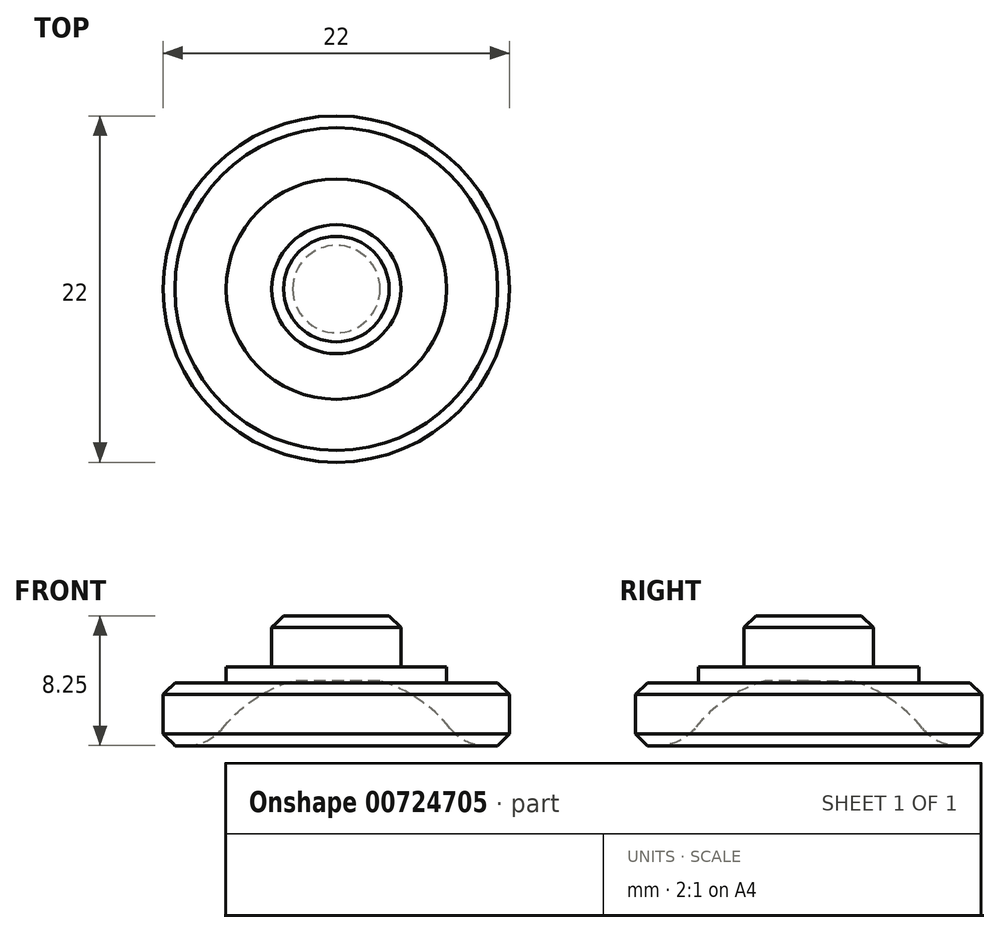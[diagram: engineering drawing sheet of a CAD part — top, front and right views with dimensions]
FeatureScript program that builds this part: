
annotation { "Feature Type Name" : "Feature", "Feature Type Description" : "" }
export const myFeature = defineFeature(function(context is Context, id is Id, definition is map)
    precondition{}
    {
        {
            var Q0;
            Q0=qCreatedBy(makeId("Front.planeOp"),FACE);
            var sketch = newSketch(context, id + "F0", { "sketchPlane" : qUnion([Q0])});
            skLineSegment(sketch, "E0", {"start": v(-11, -5.72) * mm, "end": v(-11, -1.72) * mm});
            skLineSegment(sketch, "E1", {"start": v(-11, -1.72) * mm, "end": v(-7, -1.72) * mm});
            skLineSegment(sketch, "E2", {"start": v(-7, -1.72) * mm, "end": v(-7, -0.72) * mm});
            skLineSegment(sketch, "E3", {"start": v(-7, -0.72) * mm, "end": v(-4.1, -0.72) * mm});
            skLineSegment(sketch, "E4", {"start": v(-4.1, -0.72) * mm, "end": v(-4.1, 2.53) * mm});
            skLineSegment(sketch, "E5", {"start": v(-4.1, 2.53) * mm, "end": v(0, 2.53) * mm});
            skLineSegment(sketch, "E6", {"start": v(0, 2.53) * mm, "end": v(0, -4.18) * mm});
            skLineSegment(sketch, "E7", {"start": v(-11, -5.72) * mm, "end": v(-8, -5.72) * mm});
            skPoint(sketch, "E8", {"position": v(0, -1.18) * mm});
            skArc(sketch, "E9", {"start": v(-2.78, -1.6) * mm, "mid": v(-5.77, -3.18) * mm, "end": v(-8, -5.72) * mm});
            skLineSegment(sketch, "E10", {"start": v(0, -1.18) * mm, "end": v(4, -1.18) * mm, "construction": true});
            skLineSegment(sketch, "E11", {"start": v(0, -1.6) * mm, "end": v(-2.78, -1.6) * mm});
            skSolve(sketch);
        }
        {
            var Q0;
            Q0=makeQuery(id+"F0.imprint","IMPRINT",FACE,{"disambiguationData":[TD([[makeQuery(id+"F0.imprint","IMPRINT",EDGE,{"derivedFrom":sQuery(id+"F0.wireOp",EDGE,"E0")}),-1.0]])]});
            var Q1;
            Q1=sQuery(id+"F0.wireOp",EDGE,"E6");
            revolve(context, id + "F1", {"surfaceOperationType" : NewSurfaceOperationType.NEW, "entities" : qUnion([Q0]), "axis" : qUnion([Q1]), "revolveType" : RevolveType.FULL});
        }
        {
            var Q0;
            Q0=makeQuery(id+"F1.opRevolve","SWEPT_EDGE",EDGE,{"disambiguationData":[OSD([sQuery(id+"F0.wireOp",EDGE,"E7"),sQuery(id+"F0.wireOp",EDGE,"E9")])]});
            fillet(context, id + "F2", {"entities" : qUnion([Q0]), "radius" : 3 * mm, "tangentPropagation" : true, "allowEdgeOverflow" : false});
        }
        {
            var Q0;
            Q0=makeQuery(id+"F1.opRevolve","SWEPT_EDGE",EDGE,{"disambiguationData":[OSD([sQuery(id+"F0.wireOp",EDGE,"E0"),sQuery(id+"F0.wireOp",EDGE,"E7")])]});
            var Q1;
            Q1=makeQuery(id+"F1.opRevolve","SWEPT_EDGE",EDGE,{"disambiguationData":[OSD([sQuery(id+"F0.wireOp",EDGE,"E0"),sQuery(id+"F0.wireOp",EDGE,"E1")])]});
            chamfer(context, id + "F3", {"entities" : qUnion([Q0, Q1]), "width" : .75 * mm, "tangentPropagation" : true});
        }
        {
            var Q0;
            Q0=makeQuery(id+"F1.opRevolve","SWEPT_FACE",FACE,{"disambiguationData":[OSD([sQuery(id+"F0.wireOp",EDGE,"E5")])]});
            chamfer(context, id + "F4", {"entities" : qUnion([Q0]), "width" : .75 * mm, "tangentPropagation" : true});
        }
    });
